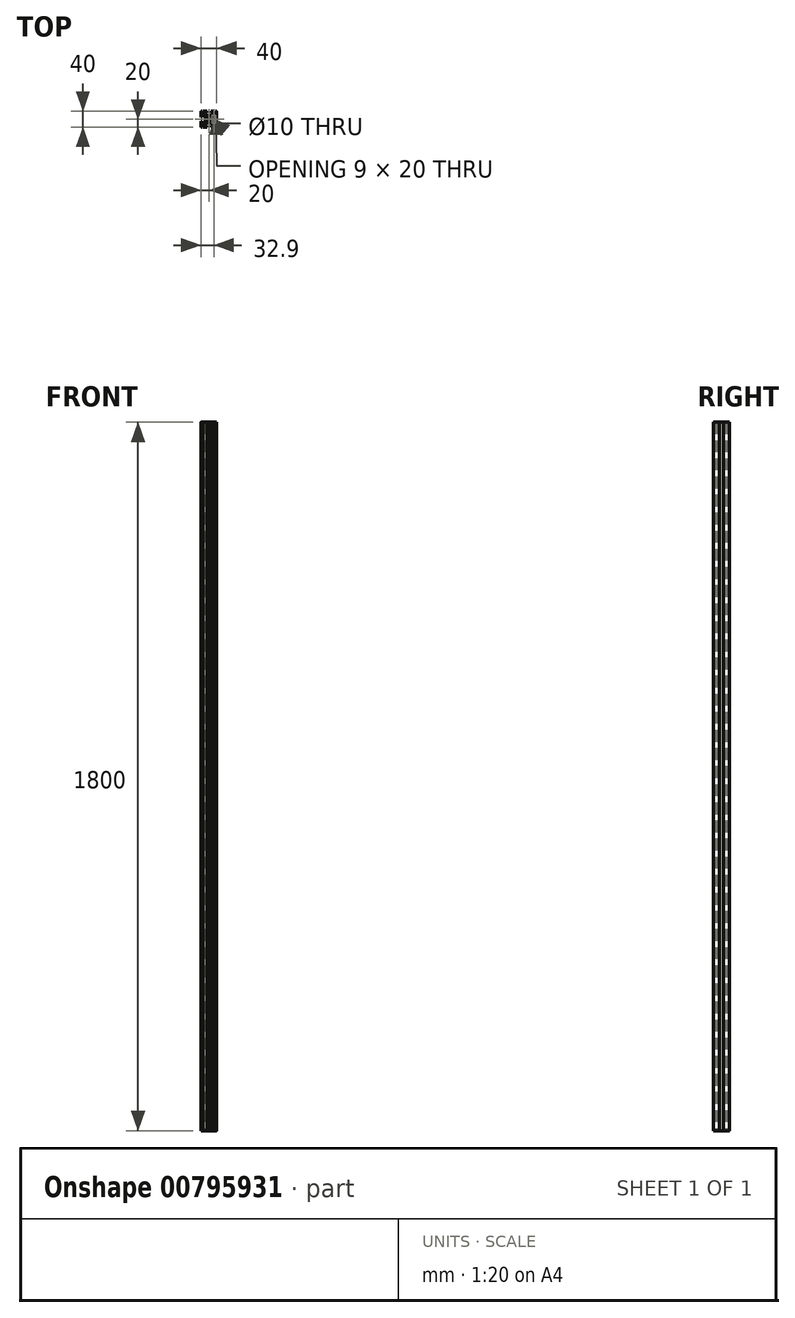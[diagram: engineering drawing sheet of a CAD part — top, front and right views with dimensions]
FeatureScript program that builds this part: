
annotation { "Feature Type Name" : "Feature", "Feature Type Description" : "" }
export const myFeature = defineFeature(function(context is Context, id is Id, definition is map)
    precondition{}
    {
        {
            var Q0;
            Q0=qCreatedBy(makeId("Top.planeOp"),FACE);
            var sketch = newSketch(context, id + "F0", { "sketchPlane" : qUnion([Q0])});
            skLineSegment(sketch, "E0", {"start": v(0, 0) * mm, "end": v(19.04, 19.04) * mm, "construction": true});
            skLineSegment(sketch, "E1", {"start": v(8.4, 0) * mm, "end": v(8.4, 3.5) * mm});
            skLineSegment(sketch, "E2", {"start": v(8.4, 3.5) * mm, "end": v(14.9, 10) * mm});
            skLineSegment(sketch, "E3", {"start": v(14.9, 10) * mm, "end": v(16.9, 10) * mm});
            skLineSegment(sketch, "E4", {"start": v(16.9, 10) * mm, "end": v(16.9, 5) * mm});
            skLineSegment(sketch, "E5", {"start": v(16.9, 5) * mm, "end": v(20, 5) * mm});
            skLineSegment(sketch, "E6", {"start": v(20, 5) * mm, "end": v(20, 5) * mm});
            skLineSegment(sketch, "E7", {"start": v(20, 5) * mm, "end": v(20, 19) * mm});
            skArc(sketch, "E8", {"start": v(20, 19) * mm, "mid": v(19.92, 19.38) * mm, "end": v(19.7, 19.7) * mm});
            skLineSegment(sketch, "E9.MirrorCS", {"start": v(5, 20) * mm, "end": v(5, 20) * mm});
            skLineSegment(sketch, "E10.MirrorCS", {"start": v(10, 14.9) * mm, "end": v(10, 16.9) * mm});
            skLineSegment(sketch, "E11.MirrorCS", {"start": v(3.5, 8.4) * mm, "end": v(10, 14.9) * mm});
            skLineSegment(sketch, "E12.MirrorCS", {"start": v(0, 8.4) * mm, "end": v(3.5, 8.4) * mm});
            skLineSegment(sketch, "E13.MirrorCS", {"start": v(10, 16.9) * mm, "end": v(5, 16.9) * mm});
            skLineSegment(sketch, "E14.MirrorCS", {"start": v(5, 16.9) * mm, "end": v(5, 20) * mm});
            skLineSegment(sketch, "E15.MirrorCS", {"start": v(5, 20) * mm, "end": v(19, 20) * mm});
            skArc(sketch, "E16.MirrorCS", {"start": v(19, 20) * mm, "mid": v(19.38, 19.92) * mm, "end": v(19.7, 19.7) * mm});
            skArc(sketch, "E17.1.0", {"start": v(-20, 19) * mm, "mid": v(-19.92, 19.38) * mm, "end": v(-19.7, 19.7) * mm});
            skLineSegment(sketch, "E17.1.1", {"start": v(-20, 5) * mm, "end": v(-20, 19) * mm});
            skLineSegment(sketch, "E17.1.2", {"start": v(-16.9, 5) * mm, "end": v(-20, 5) * mm});
            skLineSegment(sketch, "E17.1.3", {"start": v(-14.9, 10) * mm, "end": v(-16.9, 10) * mm});
            skArc(sketch, "E17.1.4", {"start": v(-19, 20) * mm, "mid": v(-19.38, 19.92) * mm, "end": v(-19.7, 19.7) * mm});
            skLineSegment(sketch, "E17.1.5", {"start": v(-5, 20) * mm, "end": v(-19, 20) * mm});
            skLineSegment(sketch, "E17.1.6", {"start": v(-5, 16.9) * mm, "end": v(-5, 20) * mm});
            skLineSegment(sketch, "E17.1.7", {"start": v(-10, 16.9) * mm, "end": v(-5, 16.9) * mm});
            skLineSegment(sketch, "E17.1.8", {"start": v(-10, 14.9) * mm, "end": v(-10, 16.9) * mm});
            skLineSegment(sketch, "E17.1.9", {"start": v(-3.5, 8.4) * mm, "end": v(-10, 14.9) * mm});
            skLineSegment(sketch, "E17.1.10", {"start": v(0, 8.4) * mm, "end": v(-3.5, 8.4) * mm});
            skLineSegment(sketch, "E17.1.11", {"start": v(0, 0) * mm, "end": v(-19.04, 19.04) * mm, "construction": true});
            skLineSegment(sketch, "E17.1.12", {"start": v(-16.9, 10) * mm, "end": v(-16.9, 5) * mm});
            skLineSegment(sketch, "E17.1.13", {"start": v(-8.4, 0) * mm, "end": v(-8.4, 3.5) * mm});
            skLineSegment(sketch, "E17.1.14", {"start": v(-8.4, 3.5) * mm, "end": v(-14.9, 10) * mm});
            skLineSegment(sketch, "E17.1.15", {"start": v(-20, 5) * mm, "end": v(-20, 5) * mm});
            skLineSegment(sketch, "E17.1.16", {"start": v(-20, 5) * mm, "end": v(-20, 5) * mm});
            skLineSegment(sketch, "E17.1.17", {"start": v(-5, 20) * mm, "end": v(-5, 20) * mm});
            skLineSegment(sketch, "E17.1.18", {"start": v(-5, 20) * mm, "end": v(-5, 20) * mm});
            skArc(sketch, "E17.2.0", {"start": v(-19, -20) * mm, "mid": v(-19.38, -19.92) * mm, "end": v(-19.7, -19.7) * mm});
            skLineSegment(sketch, "E17.2.1", {"start": v(-5, -20) * mm, "end": v(-19, -20) * mm});
            skLineSegment(sketch, "E17.2.2", {"start": v(-5, -16.9) * mm, "end": v(-5, -20) * mm});
            skLineSegment(sketch, "E17.2.3", {"start": v(-10, -14.9) * mm, "end": v(-10, -16.9) * mm});
            skArc(sketch, "E17.2.4", {"start": v(-20, -19) * mm, "mid": v(-19.92, -19.38) * mm, "end": v(-19.7, -19.7) * mm});
            skLineSegment(sketch, "E17.2.5", {"start": v(-20, -5) * mm, "end": v(-20, -19) * mm});
            skLineSegment(sketch, "E17.2.6", {"start": v(-16.9, -5) * mm, "end": v(-20, -5) * mm});
            skLineSegment(sketch, "E17.2.7", {"start": v(-16.9, -10) * mm, "end": v(-16.9, -5) * mm});
            skLineSegment(sketch, "E17.2.8", {"start": v(-14.9, -10) * mm, "end": v(-16.9, -10) * mm});
            skLineSegment(sketch, "E17.2.9", {"start": v(-8.4, -3.5) * mm, "end": v(-14.9, -10) * mm});
            skLineSegment(sketch, "E17.2.10", {"start": v(-8.4, 0) * mm, "end": v(-8.4, -3.5) * mm});
            skLineSegment(sketch, "E17.2.11", {"start": v(0, 0) * mm, "end": v(-19.04, -19.04) * mm, "construction": true});
            skLineSegment(sketch, "E17.2.12", {"start": v(-10, -16.9) * mm, "end": v(-5, -16.9) * mm});
            skLineSegment(sketch, "E17.2.13", {"start": v(0, -8.4) * mm, "end": v(-3.5, -8.4) * mm});
            skLineSegment(sketch, "E17.2.14", {"start": v(-3.5, -8.4) * mm, "end": v(-10, -14.9) * mm});
            skLineSegment(sketch, "E17.2.15", {"start": v(-5, -20) * mm, "end": v(-5, -20) * mm});
            skLineSegment(sketch, "E17.2.16", {"start": v(-5, -20) * mm, "end": v(-5, -20) * mm});
            skLineSegment(sketch, "E17.2.17", {"start": v(-20, -5) * mm, "end": v(-20, -5) * mm});
            skLineSegment(sketch, "E17.2.18", {"start": v(-20, -5) * mm, "end": v(-20, -5) * mm});
            skArc(sketch, "E17.3.0", {"start": v(20, -19) * mm, "mid": v(19.92, -19.38) * mm, "end": v(19.7, -19.7) * mm});
            skLineSegment(sketch, "E17.3.1", {"start": v(20, -5) * mm, "end": v(20, -19) * mm});
            skLineSegment(sketch, "E17.3.2", {"start": v(16.9, -5) * mm, "end": v(20, -5) * mm});
            skLineSegment(sketch, "E17.3.3", {"start": v(14.9, -10) * mm, "end": v(16.9, -10) * mm});
            skArc(sketch, "E17.3.4", {"start": v(19, -20) * mm, "mid": v(19.38, -19.92) * mm, "end": v(19.7, -19.7) * mm});
            skLineSegment(sketch, "E17.3.5", {"start": v(5, -20) * mm, "end": v(19, -20) * mm});
            skLineSegment(sketch, "E17.3.6", {"start": v(5, -16.9) * mm, "end": v(5, -20) * mm});
            skLineSegment(sketch, "E17.3.7", {"start": v(10, -16.9) * mm, "end": v(5, -16.9) * mm});
            skLineSegment(sketch, "E17.3.8", {"start": v(10, -14.9) * mm, "end": v(10, -16.9) * mm});
            skLineSegment(sketch, "E17.3.9", {"start": v(3.5, -8.4) * mm, "end": v(10, -14.9) * mm});
            skLineSegment(sketch, "E17.3.10", {"start": v(0, -8.4) * mm, "end": v(3.5, -8.4) * mm});
            skLineSegment(sketch, "E17.3.11", {"start": v(0, 0) * mm, "end": v(19.04, -19.04) * mm, "construction": true});
            skLineSegment(sketch, "E17.3.12", {"start": v(16.9, -10) * mm, "end": v(16.9, -5) * mm});
            skLineSegment(sketch, "E17.3.13", {"start": v(8.4, 0) * mm, "end": v(8.4, -3.5) * mm});
            skLineSegment(sketch, "E17.3.14", {"start": v(8.4, -3.5) * mm, "end": v(14.9, -10) * mm});
            skLineSegment(sketch, "E17.3.15", {"start": v(20, -5) * mm, "end": v(20, -5) * mm});
            skLineSegment(sketch, "E17.3.16", {"start": v(20, -5) * mm, "end": v(20, -5) * mm});
            skLineSegment(sketch, "E17.3.17", {"start": v(5, -20) * mm, "end": v(5, -20) * mm});
            skLineSegment(sketch, "E17.3.18", {"start": v(5, -20) * mm, "end": v(5, -20) * mm});
            skPoint(sketch, "E17.center", {"position": v(0, 0) * mm});
            skLineSegment(sketch, "E18.bottom", {"start": v(17.4, 5) * mm, "end": v(19.5, 5) * mm});
            skLineSegment(sketch, "E18.top", {"start": v(17.4, -5) * mm, "end": v(19.5, -5) * mm});
            skLineSegment(sketch, "E18.left", {"start": v(17.4, 5) * mm, "end": v(17.4, -5) * mm});
            skLineSegment(sketch, "E18.right", {"start": v(19.5, 5) * mm, "end": v(19.5, -5) * mm});
            skSolve(sketch);
        }
        {
            var Q0;
            Q0 = qSketchRegion(id + "F0", true);
            extrude(context, id + "F1", {"entities" : qUnion([Q0]), "depth" : 1800 * mm, "offsetDistance" : 25 * mm});
        }
        {
            var Q0;
            Q0=qCreatedBy(makeId("Top.planeOp"),FACE);
            var sketch = newSketch(context, id + "F2", { "sketchPlane" : qUnion([Q0])});
            skLineSegment(sketch, "E19", {"start": v(14.3, 20) * mm, "end": v(14.3, 15.3) * mm});
            skLineSegment(sketch, "E20", {"start": v(16.9, 15.3) * mm, "end": v(16.9, 20) * mm});
            skLineSegment(sketch, "E21", {"start": v(14.3, 20) * mm, "end": v(16.9, 20) * mm});
            skArc(sketch, "E22", {"start": v(14.3, 15.3) * mm, "mid": v(15.6, 14) * mm, "end": v(16.9, 15.3) * mm});
            skArc(sketch, "E23.MirrorCS", {"start": v(-14.3, 15.3) * mm, "mid": v(-15.6, 14) * mm, "end": v(-16.9, 15.3) * mm});
            skLineSegment(sketch, "E24.MirrorCS", {"start": v(-14.3, 20) * mm, "end": v(-16.9, 20) * mm});
            skLineSegment(sketch, "E25.MirrorCS", {"start": v(-14.3, 20) * mm, "end": v(-14.3, 15.3) * mm});
            skLineSegment(sketch, "E26.MirrorCS", {"start": v(-16.9, 15.3) * mm, "end": v(-16.9, 20) * mm});
            skLineSegment(sketch, "E27.MirrorCS", {"start": v(16.9, -15.3) * mm, "end": v(16.9, -20) * mm});
            skLineSegment(sketch, "E28.MirrorCS", {"start": v(-14.3, -20) * mm, "end": v(-14.3, -15.3) * mm});
            skLineSegment(sketch, "E29.MirrorCS", {"start": v(14.3, -20) * mm, "end": v(16.9, -20) * mm});
            skArc(sketch, "E30.MirrorCS", {"start": v(-14.3, -15.3) * mm, "mid": v(-15.6, -14) * mm, "end": v(-16.9, -15.3) * mm});
            skLineSegment(sketch, "E31.MirrorCS", {"start": v(-16.9, -15.3) * mm, "end": v(-16.9, -20) * mm});
            skArc(sketch, "E32.MirrorCS", {"start": v(14.3, -15.3) * mm, "mid": v(15.6, -14) * mm, "end": v(16.9, -15.3) * mm});
            skLineSegment(sketch, "E33.MirrorCS", {"start": v(-14.3, -20) * mm, "end": v(-16.9, -20) * mm});
            skLineSegment(sketch, "E34.MirrorCS", {"start": v(14.3, -20) * mm, "end": v(14.3, -15.3) * mm});
            skCircle(sketch, "E35", {"center": v(0, 0) * mm, "radius": 5 * mm});
            skSolve(sketch);
        }
        {
            var Q0;
            Q0 = qSketchRegion(id + "F2", true);
            extrude(context, id + "F3", {"entities" : qUnion([Q0]), "operationType" : NewBodyOperationType.REMOVE, "endBound" : BoundingType.UP_TO_NEXT, "depth" : 25 * mm, "offsetDistance" : 25 * mm});
        }
    });
